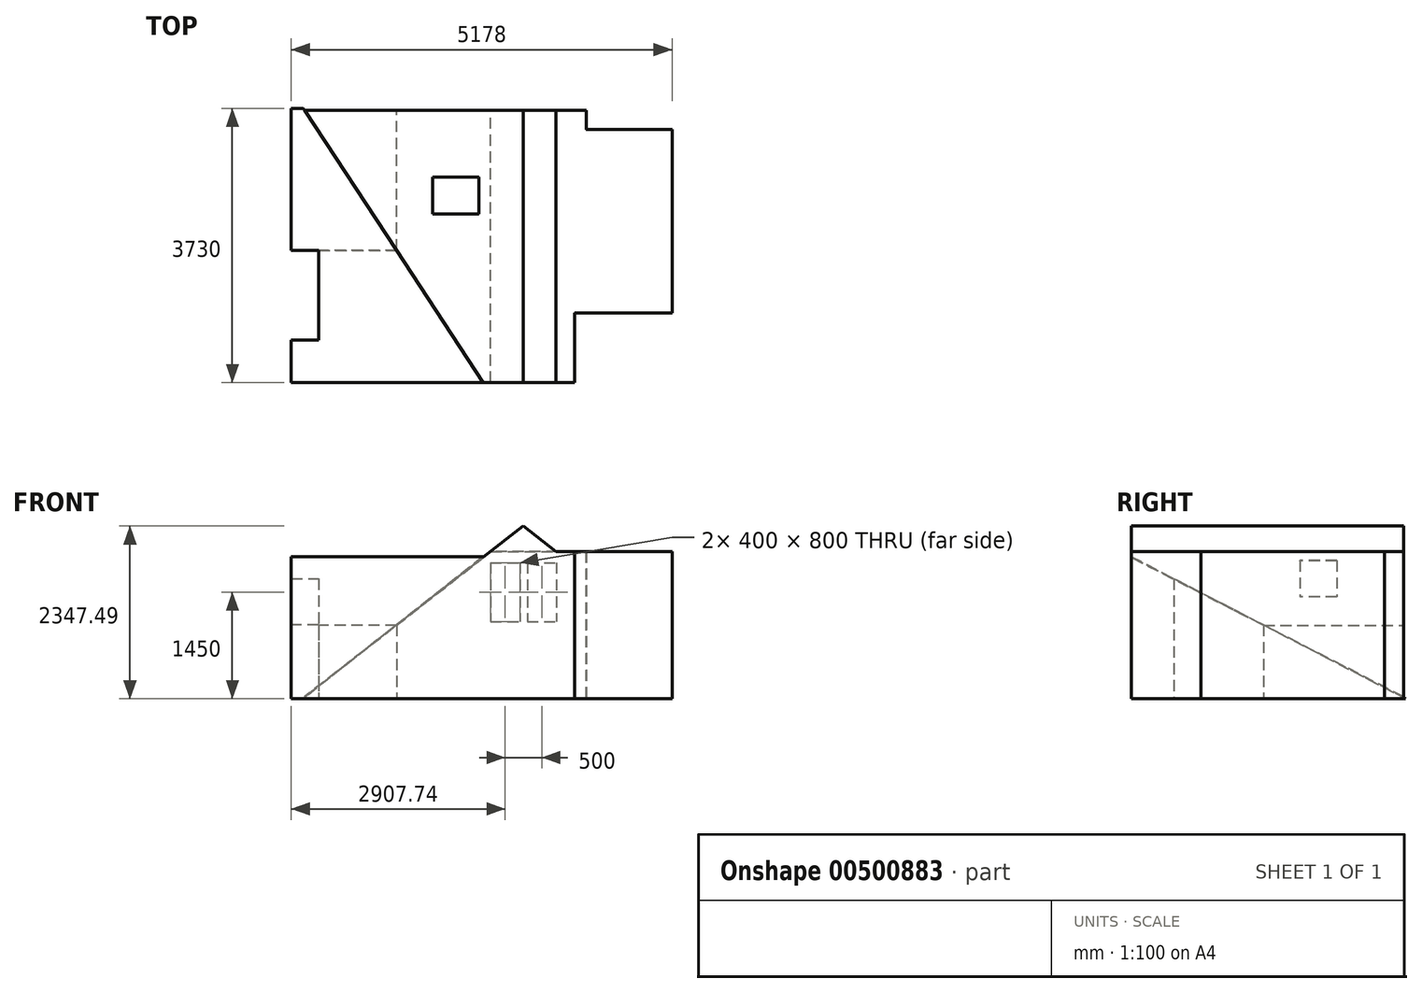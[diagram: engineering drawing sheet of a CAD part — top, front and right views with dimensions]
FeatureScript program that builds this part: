
annotation { "Feature Type Name" : "Feature", "Feature Type Description" : "" }
export const myFeature = defineFeature(function(context is Context, id is Id, definition is map)
    precondition{}
    {
        {
            var Q0;
            Q0=qCreatedBy(makeId("Top.planeOp"),FACE);
            var sketch = newSketch(context, id + "F0", { "sketchPlane" : qUnion([Q0])});
            skLineSegment(sketch, "E0", {"start": v(0, 0) * mm, "end": v(0, 580) * mm});
            skLineSegment(sketch, "E1", {"start": v(0, 580) * mm, "end": v(370, 580) * mm});
            skLineSegment(sketch, "E2", {"start": v(370, 580) * mm, "end": v(370, 1800) * mm});
            skLineSegment(sketch, "E3", {"start": v(370, 1800) * mm, "end": v(1430, 1800) * mm});
            skLineSegment(sketch, "E4", {"start": v(1430, 1800) * mm, "end": v(1430, 3700) * mm});
            skLineSegment(sketch, "E5", {"start": v(5178, 3440) * mm, "end": v(5178, 950) * mm});
            skLineSegment(sketch, "E6", {"start": v(5178, 950) * mm, "end": v(3851, 950) * mm});
            skLineSegment(sketch, "E7", {"start": v(3851, 950) * mm, "end": v(3851, 0) * mm});
            skLineSegment(sketch, "E8", {"start": v(3851, 0) * mm, "end": v(0, 0) * mm});
            skLineSegment(sketch, "E9", {"start": v(1430, 3700) * mm, "end": v(4008, 3700) * mm});
            skLineSegment(sketch, "E10", {"start": v(4008, 3700) * mm, "end": v(4008, 3440) * mm});
            skLineSegment(sketch, "E11", {"start": v(4008, 3440) * mm, "end": v(5178, 3440) * mm});
            skSolve(sketch);
        }
        {
            var Q0;
            Q0 = qSketchRegion(id + "F0", true);
            extrude(context, id + "F1", {"entities" : qUnion([Q0]), "depth" : 2000 * mm, "offsetDistance" : 25 * mm});
        }
        {
            var Q0;
            Q0=makeQuery(id+"F1.opExtrude","CAP_FACE",FACE,{"disambiguationData":[OSD([sQuery(id+"F0.wireOp",EDGE,"E0"),sQuery(id+"F0.wireOp",EDGE,"E1"),sQuery(id+"F0.wireOp",EDGE,"E2"),sQuery(id+"F0.wireOp",EDGE,"E3"),sQuery(id+"F0.wireOp",EDGE,"E4"),sQuery(id+"F0.wireOp",EDGE,"E5"),sQuery(id+"F0.wireOp",EDGE,"E6"),sQuery(id+"F0.wireOp",EDGE,"E7"),sQuery(id+"F0.wireOp",EDGE,"E8"),sQuery(id+"F0.wireOp",EDGE,"E9"),sQuery(id+"F0.wireOp",EDGE,"E10"),sQuery(id+"F0.wireOp",EDGE,"E11")])],"isStart":false});
            var sketch = newSketch(context, id + "F2", { "sketchPlane" : qUnion([Q0])});
            skLineSegment(sketch, "E12", {"start": v(2710, 3700) * mm, "end": v(2710, 0) * mm});
            skLineSegment(sketch, "E13", {"start": v(1430, 1800) * mm, "end": v(2610, 0) * mm});
            skSolve(sketch);
        }
        {
            var Q0;
            Q0=sQuery(id+"F2.wireOp",EDGE,"E13");
            cPlane(context, id + "F3", {"entities" : qUnion([Q0]), "cplaneType" : CPlaneType.LINE_ANGLE, "offset" : 25 * mm, "angle" : 90 * degree, "width" : 150 * mm, "height" : 150 * mm});
        }
        {
            var Q0;
            Q0=makeQuery(id+"F1.opExtrude","SWEPT_FACE",FACE,{"disambiguationData":[OSD([sQuery(id+"F0.wireOp",EDGE,"E9")])]});
            var sketch = newSketch(context, id + "F4", { "sketchPlane" : qUnion([Q0])});
            skLineSegment(sketch, "E14", {"start": v(-2710, 2000) * mm, "end": v(-1430, 1000) * mm});
            skLineSegment(sketch, "E15", {"start": v(-1430, 1000) * mm, "end": v(-1430, 2000) * mm});
            skLineSegment(sketch, "E16", {"start": v(-1430, 2000) * mm, "end": v(-2710, 2000) * mm});
            skSolve(sketch);
        }
        {
            var Q0;
            Q0 = qSketchRegion(id + "F4", true);
            var Q1;
            Q1=qCreatedBy(id+"F3.planeOp",FACE);
            extrude(context, id + "F5", {"entities" : qUnion([Q0]), "operationType" : NewBodyOperationType.REMOVE, "endBound" : BoundingType.UP_TO_SURFACE, "oppositeDirection" : true, "depth" : 25 * mm, "endBoundEntityFace" : qUnion([Q1]), "offsetDistance" : 25 * mm});
        }
        {
            var Q0;
            Q0=makeQuery(id+"F1.opExtrude","SWEPT_FACE",FACE,{"disambiguationData":[OSD([sQuery(id+"F0.wireOp",EDGE,"E0")])]});
            var sketch = newSketch(context, id + "F6", { "sketchPlane" : qUnion([Q0])});
            skLineSegment(sketch, "E17", {"start": v(130, 2000) * mm, "end": v(-1800, 1000) * mm});
            skLineSegment(sketch, "E18", {"start": v(-1800, 1000) * mm, "end": v(-1800, 2000) * mm});
            skLineSegment(sketch, "E19", {"start": v(-1800, 2000) * mm, "end": v(130, 2000) * mm});
            skSolve(sketch);
        }
        {
            var Q0;
            Q0 = qSketchRegion(id + "F6", true);
            var Q1;
            Q1=qCreatedBy(id+"F3.planeOp",FACE);
            extrude(context, id + "F7", {"entities" : qUnion([Q0]), "operationType" : NewBodyOperationType.REMOVE, "endBound" : BoundingType.UP_TO_SURFACE, "oppositeDirection" : true, "depth" : 25 * mm, "endBoundEntityFace" : qUnion([Q1]), "offsetDistance" : 25 * mm});
        }
        {
            var Q0;
            Q0=makeQuery(id+"F1.opExtrude","CAP_FACE",FACE,{"disambiguationData":[OSD([sQuery(id+"F0.wireOp",EDGE,"E0"),sQuery(id+"F0.wireOp",EDGE,"E1"),sQuery(id+"F0.wireOp",EDGE,"E2"),sQuery(id+"F0.wireOp",EDGE,"E3"),sQuery(id+"F0.wireOp",EDGE,"E4"),sQuery(id+"F0.wireOp",EDGE,"E5"),sQuery(id+"F0.wireOp",EDGE,"E6"),sQuery(id+"F0.wireOp",EDGE,"E7"),sQuery(id+"F0.wireOp",EDGE,"E8"),sQuery(id+"F0.wireOp",EDGE,"E9"),sQuery(id+"F0.wireOp",EDGE,"E10"),sQuery(id+"F0.wireOp",EDGE,"E11")])],"isStart":true});
            shell(context, id + "F8", {"entities" : qUnion([Q0]), "thickness" : 2.5 * mm});
        }
        {
            var Q0;
            Q0=makeQuery(id+"F1.opExtrude","SWEPT_FACE",FACE,{"disambiguationData":[OSD([sQuery(id+"F0.wireOp",EDGE,"E9")])]});
            var sketch = newSketch(context, id + "F9", { "sketchPlane" : qUnion([Q0])});
            skLineSegment(sketch, "E20.bottom", {"start": v(-2707.74, 1850) * mm, "end": v(-3107.74, 1850) * mm});
            skLineSegment(sketch, "E20.top", {"start": v(-2707.74, 1050) * mm, "end": v(-3107.74, 1050) * mm});
            skLineSegment(sketch, "E20.left", {"start": v(-2707.74, 1850) * mm, "end": v(-2707.74, 1050) * mm});
            skLineSegment(sketch, "E20.right", {"start": v(-3107.74, 1850) * mm, "end": v(-3107.74, 1050) * mm});
            skLineSegment(sketch, "E21.bottom", {"start": v(-3207.74, 1850) * mm, "end": v(-3607.74, 1850) * mm});
            skLineSegment(sketch, "E21.top", {"start": v(-3207.74, 1050) * mm, "end": v(-3607.74, 1050) * mm});
            skLineSegment(sketch, "E21.left", {"start": v(-3207.74, 1850) * mm, "end": v(-3207.74, 1050) * mm});
            skLineSegment(sketch, "E21.right", {"start": v(-3607.74, 1850) * mm, "end": v(-3607.74, 1050) * mm});
            skSolve(sketch);
        }
        {
            var Q0;
            Q0 = qSketchRegion(id + "F9", true);
            extrude(context, id + "F10", {"entities" : qUnion([Q0]), "operationType" : NewBodyOperationType.REMOVE, "endBound" : BoundingType.UP_TO_NEXT, "oppositeDirection" : true, "depth" : 25 * mm, "offsetDistance" : 25 * mm});
        }
        {
            var Q0;
            Q0=makeQuery(id+"F5.boolean.opBoolean","COPY",FACE,{"derivedFrom":makeQuery(id+"F5.opExtrude","SWEPT_FACE",FACE,{"disambiguationData":[OSD([sQuery(id+"F4.wireOp",EDGE,"E14")])]})});
            var sketch = newSketch(context, id + "F11", { "sketchPlane" : qUnion([Q0])});
            skLineSegment(sketch, "E22.bottom", {"start": v(3166.83, 2793.75) * mm, "end": v(2366.83, 2793.75) * mm});
            skLineSegment(sketch, "E22.top", {"start": v(3166.83, 2293.75) * mm, "end": v(2366.83, 2293.75) * mm});
            skLineSegment(sketch, "E22.left", {"start": v(3166.83, 2793.75) * mm, "end": v(3166.83, 2293.75) * mm});
            skLineSegment(sketch, "E22.right", {"start": v(2366.83, 2793.75) * mm, "end": v(2366.83, 2293.75) * mm});
            skSolve(sketch);
        }
        {
            var Q0;
            Q0 = qSketchRegion(id + "F11", true);
            extrude(context, id + "F12", {"entities" : qUnion([Q0]), "operationType" : NewBodyOperationType.REMOVE, "endBound" : BoundingType.UP_TO_NEXT, "oppositeDirection" : true, "depth" : 25 * mm, "offsetDistance" : 25 * mm});
        }
        {
            var Q0;
            Q0=makeQuery(id+"F1.opExtrude","SWEPT_FACE",FACE,{"disambiguationData":[OSD([sQuery(id+"F0.wireOp",EDGE,"E9")])]});
            var sketch = newSketch(context, id + "F13", { "sketchPlane" : qUnion([Q0])});
            skLineSegment(sketch, "E23", {"start": v(-1430, 1000) * mm, "end": v(-150, 0) * mm});
            skLineSegment(sketch, "E24", {"start": v(-150, 0) * mm, "end": v(-1430, 0) * mm});
            skLineSegment(sketch, "E25", {"start": v(-1430, 0) * mm, "end": v(-1430, 1000) * mm});
            skSolve(sketch);
        }
        {
            var Q0;
            Q0 = qSketchRegion(id + "F13", true);
            var Q1;
            Q1=qCreatedBy(id+"F3.planeOp",FACE);
            extrude(context, id + "F14", {"entities" : qUnion([Q0]), "operationType" : NewBodyOperationType.ADD, "endBound" : BoundingType.UP_TO_SURFACE, "oppositeDirection" : true, "depth" : 25 * mm, "endBoundEntityFace" : qUnion([Q1]), "offsetDistance" : 25 * mm});
        }
        {
            var Q0;
            Q0=makeQuery(id+"F1.opExtrude","SWEPT_FACE",FACE,{"disambiguationData":[OSD([sQuery(id+"F0.wireOp",EDGE,"E2")])]});
            var sketch = newSketch(context, id + "F15", { "sketchPlane" : qUnion([Q0])});
            skLineSegment(sketch, "E26", {"start": v(-1800, 1000) * mm, "end": v(-3730, 0) * mm});
            skLineSegment(sketch, "E27", {"start": v(-3730, 0) * mm, "end": v(-1800, 0) * mm});
            skLineSegment(sketch, "E28", {"start": v(-1800, 0) * mm, "end": v(-1800, 1000) * mm});
            skSolve(sketch);
        }
        {
            var Q0;
            Q0 = qSketchRegion(id + "F15", true);
            var Q1;
            Q1=qCreatedBy(id+"F3.planeOp",FACE);
            var Q2;
            Q2=makeQuery(id+"F1.opExtrude","SWEPT_FACE",FACE,{"disambiguationData":[OSD([sQuery(id+"F0.wireOp",EDGE,"E0")])]});
            extrude(context, id + "F16", {"entities" : qUnion([Q0]), "operationType" : NewBodyOperationType.ADD, "endBound" : BoundingType.UP_TO_SURFACE, "oppositeDirection" : true, "depth" : 25 * mm, "endBoundEntityFace" : qUnion([Q1]), "offsetDistance" : 25 * mm, "hasSecondDirection" : true, "secondDirectionBound" : SecondDirectionBoundingType.UP_TO_SURFACE, "secondDirectionOppositeDirection" : false, "secondDirectionDepth" : 25 * mm, "secondDirectionBoundEntityFace" : qUnion([Q2])});
        }
        {
            var Q0;
            Q0=makeQuery(id+"F14.boolean.opBoolean","MERGE",FACE,{"derivedFrom":[makeQuery(id+"F1.opExtrude","SWEPT_FACE",FACE,{"disambiguationData":[OSD([sQuery(id+"F0.wireOp",EDGE,"E9")])]}),makeQuery(id+"F14.opExtrude","CAP_FACE",FACE,{"disambiguationData":[OSD([sQuery(id+"F13.wireOp",EDGE,"E23"),sQuery(id+"F13.wireOp",EDGE,"E24"),sQuery(id+"F13.wireOp",EDGE,"E25")])],"isStart":true})]});
            var sketch = newSketch(context, id + "F17", { "sketchPlane" : qUnion([Q0])});
            skLineSegment(sketch, "E29", {"start": v(-2710, 2000) * mm, "end": v(-3154.79, 2347.5) * mm});
            skLineSegment(sketch, "E30", {"start": v(-3154.79, 2347.5) * mm, "end": v(-3599.57, 2000) * mm});
            skLineSegment(sketch, "E31", {"start": v(-3599.57, 2000) * mm, "end": v(-2710, 2000) * mm});
            skSolve(sketch);
        }
        {
            var Q0;
            Q0 = qSketchRegion(id + "F17", true);
            var Q1;
            Q1=makeQuery(id+"F1.opExtrude","SWEPT_FACE",FACE,{"disambiguationData":[OSD([sQuery(id+"F0.wireOp",EDGE,"E8")])]});
            extrude(context, id + "F18", {"entities" : qUnion([Q0]), "operationType" : NewBodyOperationType.ADD, "endBound" : BoundingType.UP_TO_SURFACE, "oppositeDirection" : true, "depth" : 25 * mm, "endBoundEntityFace" : qUnion([Q1]), "offsetDistance" : 25 * mm});
        }
    });
